# Revit family: Krowne_HS-1419_Drop-in_UnderbarSink
name_source: partatom
category: Plumbing Fixtures
revit_build: Autodesk Revit 2018 (Build: 20190510_1515(x64)
units: mm (PartAtom-declared; Revit-internal decimal feet)

## family parameters
Always vertical = Yes
Cut with Voids When Loaded = Yes
OmniClass Number = 23.40.40.14.24.11
OmniClass Title = Bar Equipment
Part Type = Normal
Room Calculation Point = No
Round Connector Dimension = Use Diameter
Shared = No
Work Plane-Based = Yes

## types (1)
- DefaultType
    Assembly Code = E1090320
    CSI MasterFormat = 11 46 13
    Cold Water Connection Height = 29"
    Cold Water Maximum Pressure = 0.00 psi
    Cold Water Minimum Pressure = 0.00 psi
    Cold Water Size = 1"
    Cold Water Temperature Recommended = 70 °F
    Default Elevation = 48"
    Depth = 18"
    Description = Drop-In Sink
    Foodservice Equipment Identifier = Yes
    Hot Water Connection Height = 29"
    Hot Water Maximum Pressure = 0.00 psi
    Hot Water Minimum Pressure = 0.00 psi
    Hot Water Size = 1"
    Hot Water Temperature = 100 °F
    Indirect Waste Connection Height = 18"
    Indirect Waste Size = 4"
    KCL SpecSheet URL = http://kclweb.kclcad.com
    KCLRef = KCL2C9,,00057cc6-0000-0000-0000-000000000307,KR,HS-1419 ,636971080020000000,e514fae7-dcac-4b39-8c8a-837ae4aa0b21,205d522f-03fe-446f-8676-9bec7d274316
    Manufacturer = Krowne Metal
    Model = HS-1419
    Sink Depth = 14"
    Sink Width = 10"
    URL = www.krowne.com
    Weight in Pounds = 16
    Width = 12"

## geometry (parser evidence)
native form markers: Sweep x1
no freeform markers — native parametric forms only
